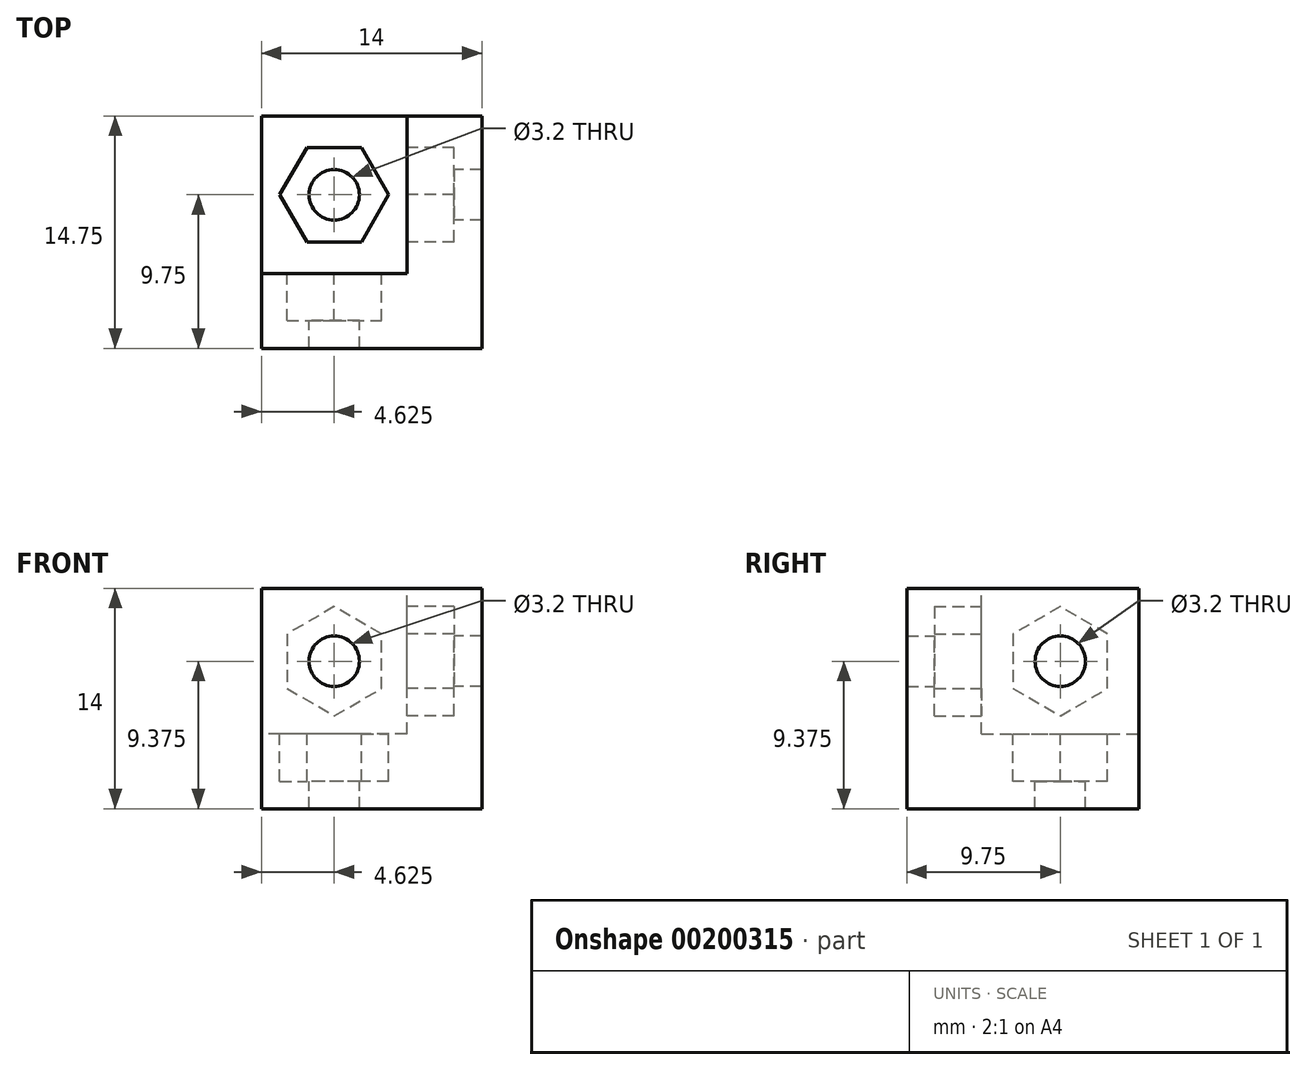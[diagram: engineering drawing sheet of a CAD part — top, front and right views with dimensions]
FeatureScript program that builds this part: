
annotation { "Feature Type Name" : "Feature", "Feature Type Description" : "" }
export const myFeature = defineFeature(function(context is Context, id is Id, definition is map)
    precondition{}
    {
        {
            var Q0;
            Q0=qCreatedBy(makeId("Front.planeOp"),FACE);
            var sketch = newSketch(context, id + "F0", { "sketchPlane" : qUnion([Q0])});
            skLineSegment(sketch, "E0", {"start": v(0, 0) * mm, "end": v(-14, 0) * mm});
            skLineSegment(sketch, "E1", {"start": v(0, 0) * mm, "end": v(0, 14) * mm});
            skLineSegment(sketch, "E2.0", {"start": v(-4.75, 4.75) * mm, "end": v(-4.75, 14) * mm});
            skLineSegment(sketch, "E2.1", {"start": v(-4.75, 4.75) * mm, "end": v(-14, 4.75) * mm});
            skLineSegment(sketch, "E3", {"start": v(-14, 4.75) * mm, "end": v(-14, 0) * mm});
            skLineSegment(sketch, "E4", {"start": v(-4.75, 14) * mm, "end": v(0, 14) * mm});
            skSolve(sketch);
        }
        {
            var Q0;
            Q0=makeQuery(id+"F0.imprint","IMPRINT",FACE,{"disambiguationData":[TD([[makeQuery(id+"F0.imprint","IMPRINT",EDGE,{"derivedFrom":sQuery(id+"F0.wireOp",EDGE,"E0")}),-1.0]])]});
            extrude(context, id + "F1", {"entities" : qUnion([Q0]), "depth" : 10 * mm});
        }
        {
            var Q0;
            Q0=makeQuery(id+"F1.opExtrude","SWEPT_FACE",FACE,{"disambiguationData":[OSD([sQuery(id+"F0.wireOp",EDGE,"E2.0")])]});
            var sketch = newSketch(context, id + "F2", { "sketchPlane" : qUnion([Q0])});
            skLineSegment(sketch, "E5", {"start": v(10, 9.38) * mm, "end": v(0, 9.38) * mm, "construction": true});
            skLineSegment(sketch, "E6", {"start": v(5, 14) * mm, "end": v(5, 4.75) * mm, "construction": true});
            skCircle(sketch, "E7", {"center": v(5, 9.38) * mm, "radius": 3 * mm, "construction": true});
            skCircle(sketch, "E8", {"center": v(5, 9.38) * mm, "radius": 1.6 * mm});
            skLineSegment(sketch, "E9.0", {"start": v(2, 7.64) * mm, "end": v(2, 11.1) * mm});
            skLineSegment(sketch, "E9.1", {"start": v(2, 11.1) * mm, "end": v(5, 12.84) * mm});
            skLineSegment(sketch, "E9.2", {"start": v(5, 12.84) * mm, "end": v(8, 11.1) * mm});
            skLineSegment(sketch, "E9.3", {"start": v(8, 11.1) * mm, "end": v(8, 7.64) * mm});
            skLineSegment(sketch, "E9.4", {"start": v(8, 7.64) * mm, "end": v(5, 5.91) * mm});
            skLineSegment(sketch, "E9.5", {"start": v(5, 5.91) * mm, "end": v(2, 7.64) * mm});
            skPoint(sketch, "E9.0.midPoint", {"position": v(2, 9.38) * mm});
            skSolve(sketch);
        }
        {
            var Q0;
            Q0=makeQuery(id+"F2.imprint","IMPRINT",FACE,{"disambiguationData":[TD([[makeQuery(id+"F2.imprint","IMPRINT",EDGE,{"derivedFrom":sQuery(id+"F2.wireOp",EDGE,"E8")}),-1.0]])]});
            extrude(context, id + "F3", {"entities" : qUnion([Q0]), "operationType" : NewBodyOperationType.REMOVE, "oppositeDirection" : true, "depth" : 3 * mm});
        }
        {
            var Q0;
            Q0=makeQuery(id+"F3.boolean.opBoolean","SPLIT",FACE,{"disambiguationData":[TD([makeQuery(id+"F3.opExtrude","SWEPT_FACE",FACE,{"disambiguationData":[OSD([sQuery(id+"F2.wireOp",EDGE,"E8")])]})])],"derivedFrom":makeQuery(id+"F1.opExtrude","SWEPT_FACE",FACE,{"disambiguationData":[OSD([sQuery(id+"F0.wireOp",EDGE,"E2.0")])]})});
            extrude(context, id + "F4", {"entities" : qUnion([Q0]), "operationType" : NewBodyOperationType.REMOVE, "oppositeDirection" : true, "depth" : 25 * mm});
        }
        {
            var Q0;
            Q0=makeQuery(id+"F1.opExtrude","SWEPT_FACE",FACE,{"disambiguationData":[OSD([sQuery(id+"F0.wireOp",EDGE,"E2.1")])]});
            var sketch = newSketch(context, id + "F5", { "sketchPlane" : qUnion([Q0])});
            skLineSegment(sketch, "E10", {"start": v(-9.38, 0) * mm, "end": v(-9.37, -10) * mm, "construction": true});
            skCircle(sketch, "E11", {"center": v(-9.38, -5) * mm, "radius": 1.6 * mm});
            skCircle(sketch, "E12", {"center": v(-9.38, -5) * mm, "radius": 3 * mm, "construction": true});
            skLineSegment(sketch, "E13.0", {"start": v(-7.64, -8) * mm, "end": v(-11.1, -8) * mm});
            skLineSegment(sketch, "E13.1", {"start": v(-11.1, -8) * mm, "end": v(-12.84, -5) * mm});
            skLineSegment(sketch, "E13.2", {"start": v(-12.84, -5) * mm, "end": v(-11.1, -2) * mm});
            skLineSegment(sketch, "E13.3", {"start": v(-11.1, -2) * mm, "end": v(-7.64, -2) * mm});
            skLineSegment(sketch, "E13.4", {"start": v(-7.64, -2) * mm, "end": v(-5.91, -5) * mm});
            skLineSegment(sketch, "E13.5", {"start": v(-5.91, -5) * mm, "end": v(-7.64, -8) * mm});
            skPoint(sketch, "E13.0.midPoint", {"position": v(-9.38, -8) * mm});
            skSolve(sketch);
        }
        {
            var Q0;
            Q0=makeQuery(id+"F5.imprint","IMPRINT",FACE,{"disambiguationData":[TD([[makeQuery(id+"F5.imprint","IMPRINT",EDGE,{"derivedFrom":sQuery(id+"F5.wireOp",EDGE,"E11")}),-1.0]])]});
            extrude(context, id + "F6", {"entities" : qUnion([Q0]), "operationType" : NewBodyOperationType.REMOVE, "oppositeDirection" : true, "depth" : 3 * mm});
        }
        {
            var Q0;
            Q0=makeQuery(id+"F6.boolean.opBoolean","SPLIT",FACE,{"disambiguationData":[TD([makeQuery(id+"F6.opExtrude","SWEPT_FACE",FACE,{"disambiguationData":[OSD([sQuery(id+"F5.wireOp",EDGE,"E11")])]})])],"derivedFrom":makeQuery(id+"F1.opExtrude","SWEPT_FACE",FACE,{"disambiguationData":[OSD([sQuery(id+"F0.wireOp",EDGE,"E2.1")])]})});
            extrude(context, id + "F7", {"entities" : qUnion([Q0]), "operationType" : NewBodyOperationType.REMOVE, "oppositeDirection" : true, "depth" : 25 * mm});
        }
        {
            var Q0;
            Q0=makeQuery(id+"F1.opExtrude","CAP_FACE",FACE,{"disambiguationData":[OSD([sQuery(id+"F0.wireOp",EDGE,"E0"),sQuery(id+"F0.wireOp",EDGE,"E1"),sQuery(id+"F0.wireOp",EDGE,"E2.0"),sQuery(id+"F0.wireOp",EDGE,"E2.1"),sQuery(id+"F0.wireOp",EDGE,"E3"),sQuery(id+"F0.wireOp",EDGE,"E4")])],"isStart":false});
            var sketch = newSketch(context, id + "F8", { "sketchPlane" : qUnion([Q0])});
            skLineSegment(sketch, "E14.bottom", {"start": v(0, 0) * mm, "end": v(-14, 0) * mm});
            skLineSegment(sketch, "E14.top", {"start": v(0, 14) * mm, "end": v(-14, 14) * mm});
            skLineSegment(sketch, "E14.left", {"start": v(0, 0) * mm, "end": v(0, 14) * mm});
            skLineSegment(sketch, "E14.right", {"start": v(-14, 0) * mm, "end": v(-14, 14) * mm});
            skSolve(sketch);
        }
        {
            var Q0;
            {var subQ1=makeQuery(id+"F1.opExtrude","CAP_EDGE",EDGE,{"disambiguationData":[OSD([sQuery(id+"F0.wireOp",EDGE,"E2.0")])],"isStart":false});Q0=makeQuery(id+"F8.imprint","IMPRINT",FACE,{"disambiguationData":[TD([[makeQuery(id+"F8.imprint","IMPRINT",EDGE,{"derivedFrom":subQ1}),1.0]])]});}
            var Q1;
            {var subQ1=sQuery(id+"F8.wireOp",EDGE,"E14.bottom");Q1=makeQuery(id+"F8.imprint","IMPRINT",FACE,{"disambiguationData":[TD([[makeQuery(id+"F8.imprint","IMPRINT",EDGE,{"derivedFrom":subQ1}),-1.0]])]});}
            extrude(context, id + "F9", {"entities" : qUnion([Q0, Q1]), "operationType" : NewBodyOperationType.ADD, "depth" : 4.75 * mm});
        }
        {
            var Q0;
            Q0=makeQuery(id+"F9.opExtrude","CAP_FACE",FACE,{"disambiguationData":[OSD([sQuery(id+"F8.wireOp",EDGE,"E14.bottom"),sQuery(id+"F8.wireOp",EDGE,"E14.top"),sQuery(id+"F8.wireOp",EDGE,"E14.left"),sQuery(id+"F8.wireOp",EDGE,"E14.right")])],"isStart":true});
            var sketch = newSketch(context, id + "F10", { "sketchPlane" : qUnion([Q0])});
            skLineSegment(sketch, "E15", {"start": v(4.75, 9.37) * mm, "end": v(14, 9.38) * mm, "construction": true});
            skCircle(sketch, "E16", {"center": v(9.38, 9.37) * mm, "radius": 1.6 * mm});
            skCircle(sketch, "E17", {"center": v(9.38, 9.37) * mm, "radius": 3 * mm, "construction": true});
            skLineSegment(sketch, "E18.0", {"start": v(6.38, 7.64) * mm, "end": v(6.37, 11.1) * mm});
            skLineSegment(sketch, "E18.1", {"start": v(6.37, 11.1) * mm, "end": v(9.37, 12.84) * mm});
            skLineSegment(sketch, "E18.2", {"start": v(9.37, 12.84) * mm, "end": v(12.38, 11.1) * mm});
            skLineSegment(sketch, "E18.3", {"start": v(12.38, 11.1) * mm, "end": v(12.38, 7.64) * mm});
            skLineSegment(sketch, "E18.4", {"start": v(12.38, 7.64) * mm, "end": v(9.38, 5.91) * mm});
            skLineSegment(sketch, "E18.5", {"start": v(9.38, 5.91) * mm, "end": v(6.38, 7.64) * mm});
            skPoint(sketch, "E18.0.midPoint", {"position": v(6.38, 9.37) * mm});
            skSolve(sketch);
        }
        {
            var Q0;
            Q0=makeQuery(id+"F10.imprint","IMPRINT",FACE,{"disambiguationData":[TD([[makeQuery(id+"F10.imprint","IMPRINT",EDGE,{"derivedFrom":sQuery(id+"F10.wireOp",EDGE,"E16")}),-1.0]])]});
            extrude(context, id + "F11", {"entities" : qUnion([Q0]), "operationType" : NewBodyOperationType.REMOVE, "oppositeDirection" : true, "depth" : 3 * mm});
        }
        {
            var Q0;
            Q0=makeQuery(id+"F11.boolean.opBoolean","SPLIT",FACE,{"disambiguationData":[TD([makeQuery(id+"F11.opExtrude","SWEPT_FACE",FACE,{"disambiguationData":[OSD([sQuery(id+"F10.wireOp",EDGE,"E16")])]})])],"derivedFrom":makeQuery(id+"F9.opExtrude","CAP_FACE",FACE,{"disambiguationData":[OSD([sQuery(id+"F8.wireOp",EDGE,"E14.bottom"),sQuery(id+"F8.wireOp",EDGE,"E14.top"),sQuery(id+"F8.wireOp",EDGE,"E14.left"),sQuery(id+"F8.wireOp",EDGE,"E14.right")])],"isStart":true})});
            extrude(context, id + "F12", {"entities" : qUnion([Q0]), "operationType" : NewBodyOperationType.REMOVE, "oppositeDirection" : true, "depth" : 25 * mm});
        }
    });
